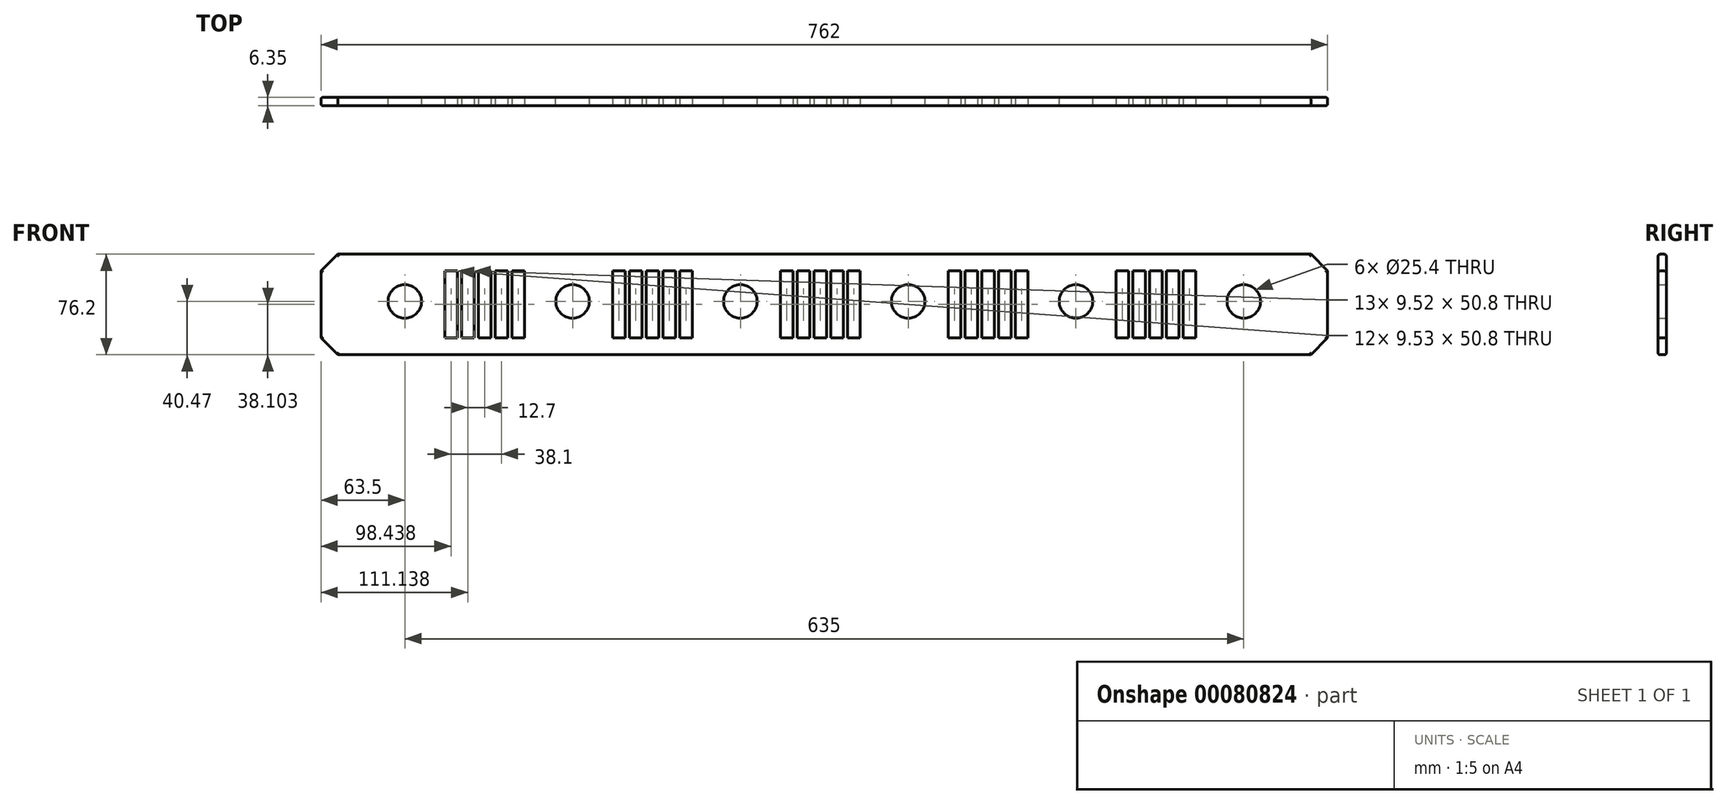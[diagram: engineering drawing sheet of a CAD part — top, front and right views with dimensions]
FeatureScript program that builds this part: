
annotation { "Feature Type Name" : "Feature", "Feature Type Description" : "" }
export const myFeature = defineFeature(function(context is Context, id is Id, definition is map)
    precondition{}
    {
        {
            var Q0;
            Q0=qCreatedBy(makeId("Front.planeOp"),FACE);
            var sketch = newSketch(context, id + "F0", { "sketchPlane" : qUnion([Q0])});
            skLineSegment(sketch, "E0.bottom", {"start": v(-63.5, 35.73) * mm, "end": v(698.5, 35.73) * mm});
            skLineSegment(sketch, "E0.top", {"start": v(-63.5, -40.47) * mm, "end": v(698.5, -40.47) * mm});
            skLineSegment(sketch, "E0.left", {"start": v(-63.5, 35.73) * mm, "end": v(-63.5, -40.47) * mm});
            skLineSegment(sketch, "E0.right", {"start": v(698.5, 35.73) * mm, "end": v(698.5, -40.47) * mm});
            skCircle(sketch, "E1", {"center": v(0, 0) * mm, "radius": 12.7 * mm});
            skCircle(sketch, "E2", {"center": v(127, 0) * mm, "radius": 12.7 * mm});
            skCircle(sketch, "E3", {"center": v(254, 0) * mm, "radius": 12.7 * mm});
            skCircle(sketch, "E4", {"center": v(381, 0) * mm, "radius": 12.7 * mm});
            skCircle(sketch, "E5", {"center": v(508, 0) * mm, "radius": 12.7 * mm});
            skCircle(sketch, "E6", {"center": v(635, 0) * mm, "radius": 12.7 * mm});
            skSolve(sketch);
        }
        {
            var Q0;
            Q0 = qSketchRegion(id + "F0", true);
            extrude(context, id + "F1", {"entities" : qUnion([Q0]), "depth" : 6.35 * mm});
        }
        {
            var Q0;
            Q0=makeQuery(id+"F1.opExtrude","CAP_FACE",FACE,{"disambiguationData":[OSD([sQuery(id+"F0.wireOp",EDGE,"E0.bottom"),sQuery(id+"F0.wireOp",EDGE,"E0.top"),sQuery(id+"F0.wireOp",EDGE,"E0.left"),sQuery(id+"F0.wireOp",EDGE,"E0.right"),sQuery(id+"F0.wireOp",EDGE,"E1"),sQuery(id+"F0.wireOp",EDGE,"E2"),sQuery(id+"F0.wireOp",EDGE,"E3"),sQuery(id+"F0.wireOp",EDGE,"E4"),sQuery(id+"F0.wireOp",EDGE,"E5"),sQuery(id+"F0.wireOp",EDGE,"E6")])],"isStart":false});
            var sketch = newSketch(context, id + "F2", { "sketchPlane" : qUnion([Q0])});
            skLineSegment(sketch, "E7.bottom", {"start": v(30.18, 23.03) * mm, "end": v(39.7, 23.03) * mm});
            skLineSegment(sketch, "E7.top", {"start": v(30.18, -27.77) * mm, "end": v(39.7, -27.77) * mm});
            skLineSegment(sketch, "E7.left", {"start": v(30.18, 23.03) * mm, "end": v(30.18, -27.77) * mm});
            skLineSegment(sketch, "E7.right", {"start": v(39.7, 23.03) * mm, "end": v(39.7, -27.77) * mm});
            skLineSegment(sketch, "E8.1.0.0", {"start": v(42.88, -27.77) * mm, "end": v(52.4, -27.77) * mm});
            skLineSegment(sketch, "E8.1.0.1", {"start": v(42.88, 23.03) * mm, "end": v(52.4, 23.03) * mm});
            skLineSegment(sketch, "E8.1.0.2", {"start": v(42.88, 23.03) * mm, "end": v(42.88, -27.77) * mm});
            skLineSegment(sketch, "E8.1.0.3", {"start": v(52.4, 23.03) * mm, "end": v(52.4, -27.77) * mm});
            skLineSegment(sketch, "E8.2.0.0", {"start": v(55.58, -27.77) * mm, "end": v(65.1, -27.77) * mm});
            skLineSegment(sketch, "E8.2.0.1", {"start": v(55.58, 23.03) * mm, "end": v(65.1, 23.03) * mm});
            skLineSegment(sketch, "E8.2.0.2", {"start": v(55.58, 23.03) * mm, "end": v(55.58, -27.77) * mm});
            skLineSegment(sketch, "E8.2.0.3", {"start": v(65.1, 23.03) * mm, "end": v(65.1, -27.77) * mm});
            skLineSegment(sketch, "E8.direction1", {"start": v(30.18, -27.77) * mm, "end": v(42.88, -27.77) * mm, "construction": true});
            skLineSegment(sketch, "E9.0.3.0", {"start": v(68.28, -27.77) * mm, "end": v(77.8, -27.77) * mm});
            skLineSegment(sketch, "E9.3.3.0", {"start": v(68.28, 23.03) * mm, "end": v(77.8, 23.03) * mm});
            skLineSegment(sketch, "E9.6.3.0", {"start": v(68.28, 23.03) * mm, "end": v(68.28, -27.77) * mm});
            skLineSegment(sketch, "E9.9.3.0", {"start": v(77.8, 23.03) * mm, "end": v(77.8, -27.77) * mm});
            skLineSegment(sketch, "E9.0.4.0", {"start": v(80.98, -27.77) * mm, "end": v(90.5, -27.77) * mm});
            skLineSegment(sketch, "E9.3.4.0", {"start": v(80.98, 23.03) * mm, "end": v(90.5, 23.03) * mm});
            skLineSegment(sketch, "E9.6.4.0", {"start": v(80.98, 23.03) * mm, "end": v(80.98, -27.77) * mm});
            skLineSegment(sketch, "E9.9.4.0", {"start": v(90.5, 23.03) * mm, "end": v(90.5, -27.77) * mm});
            skLineSegment(sketch, "E10.bottom", {"start": v(157.18, 23.03) * mm, "end": v(166.7, 23.03) * mm});
            skLineSegment(sketch, "E10.top", {"start": v(157.18, -27.77) * mm, "end": v(166.7, -27.77) * mm});
            skLineSegment(sketch, "E10.left", {"start": v(157.18, 23.03) * mm, "end": v(157.18, -27.77) * mm});
            skLineSegment(sketch, "E10.right", {"start": v(166.7, 23.03) * mm, "end": v(166.7, -27.77) * mm});
            skLineSegment(sketch, "E11.1.0.0", {"start": v(169.88, -27.77) * mm, "end": v(179.4, -27.77) * mm});
            skLineSegment(sketch, "E11.1.0.1", {"start": v(169.88, 23.03) * mm, "end": v(179.4, 23.03) * mm});
            skLineSegment(sketch, "E11.1.0.2", {"start": v(169.88, 23.03) * mm, "end": v(169.88, -27.77) * mm});
            skLineSegment(sketch, "E11.1.0.3", {"start": v(179.4, 23.03) * mm, "end": v(179.4, -27.77) * mm});
            skLineSegment(sketch, "E11.2.0.0", {"start": v(182.58, -27.77) * mm, "end": v(192.1, -27.77) * mm});
            skLineSegment(sketch, "E11.2.0.1", {"start": v(182.58, 23.03) * mm, "end": v(192.1, 23.03) * mm});
            skLineSegment(sketch, "E11.2.0.2", {"start": v(182.58, 23.03) * mm, "end": v(182.58, -27.77) * mm});
            skLineSegment(sketch, "E11.2.0.3", {"start": v(192.1, 23.03) * mm, "end": v(192.1, -27.77) * mm});
            skLineSegment(sketch, "E11.direction1", {"start": v(157.18, -27.77) * mm, "end": v(169.88, -27.77) * mm, "construction": true});
            skLineSegment(sketch, "E12.0.3.0", {"start": v(195.28, -27.77) * mm, "end": v(204.8, -27.77) * mm});
            skLineSegment(sketch, "E12.3.3.0", {"start": v(195.28, 23.03) * mm, "end": v(204.8, 23.03) * mm});
            skLineSegment(sketch, "E12.6.3.0", {"start": v(195.28, 23.03) * mm, "end": v(195.28, -27.77) * mm});
            skLineSegment(sketch, "E12.9.3.0", {"start": v(204.8, 23.03) * mm, "end": v(204.8, -27.77) * mm});
            skLineSegment(sketch, "E12.0.4.0", {"start": v(207.98, -27.77) * mm, "end": v(217.5, -27.77) * mm});
            skLineSegment(sketch, "E12.3.4.0", {"start": v(207.98, 23.03) * mm, "end": v(217.5, 23.03) * mm});
            skLineSegment(sketch, "E12.6.4.0", {"start": v(207.98, 23.03) * mm, "end": v(207.98, -27.77) * mm});
            skLineSegment(sketch, "E12.9.4.0", {"start": v(217.5, 23.03) * mm, "end": v(217.5, -27.77) * mm});
            skLineSegment(sketch, "E13.bottom", {"start": v(284.18, 23.03) * mm, "end": v(293.7, 23.03) * mm});
            skLineSegment(sketch, "E13.top", {"start": v(284.18, -27.77) * mm, "end": v(293.7, -27.77) * mm});
            skLineSegment(sketch, "E13.left", {"start": v(284.18, 23.03) * mm, "end": v(284.18, -27.77) * mm});
            skLineSegment(sketch, "E13.right", {"start": v(293.7, 23.03) * mm, "end": v(293.7, -27.77) * mm});
            skLineSegment(sketch, "E14.1.0.0", {"start": v(296.88, -27.77) * mm, "end": v(306.4, -27.77) * mm});
            skLineSegment(sketch, "E14.1.0.1", {"start": v(296.88, 23.03) * mm, "end": v(306.4, 23.03) * mm});
            skLineSegment(sketch, "E14.1.0.2", {"start": v(296.88, 23.03) * mm, "end": v(296.88, -27.77) * mm});
            skLineSegment(sketch, "E14.1.0.3", {"start": v(306.4, 23.03) * mm, "end": v(306.4, -27.77) * mm});
            skLineSegment(sketch, "E14.2.0.0", {"start": v(309.58, -27.77) * mm, "end": v(319.1, -27.77) * mm});
            skLineSegment(sketch, "E14.2.0.1", {"start": v(309.58, 23.03) * mm, "end": v(319.1, 23.03) * mm});
            skLineSegment(sketch, "E14.2.0.2", {"start": v(309.58, 23.03) * mm, "end": v(309.58, -27.77) * mm});
            skLineSegment(sketch, "E14.2.0.3", {"start": v(319.1, 23.03) * mm, "end": v(319.1, -27.77) * mm});
            skLineSegment(sketch, "E14.direction1", {"start": v(284.18, -27.77) * mm, "end": v(296.88, -27.77) * mm, "construction": true});
            skLineSegment(sketch, "E15.0.3.0", {"start": v(322.28, -27.77) * mm, "end": v(331.8, -27.77) * mm});
            skLineSegment(sketch, "E15.3.3.0", {"start": v(322.28, 23.03) * mm, "end": v(331.8, 23.03) * mm});
            skLineSegment(sketch, "E15.6.3.0", {"start": v(322.28, 23.03) * mm, "end": v(322.28, -27.77) * mm});
            skLineSegment(sketch, "E15.9.3.0", {"start": v(331.8, 23.03) * mm, "end": v(331.8, -27.77) * mm});
            skLineSegment(sketch, "E15.0.4.0", {"start": v(334.98, -27.77) * mm, "end": v(344.5, -27.77) * mm});
            skLineSegment(sketch, "E15.3.4.0", {"start": v(334.98, 23.03) * mm, "end": v(344.5, 23.03) * mm});
            skLineSegment(sketch, "E15.6.4.0", {"start": v(334.98, 23.03) * mm, "end": v(334.98, -27.77) * mm});
            skLineSegment(sketch, "E15.9.4.0", {"start": v(344.5, 23.03) * mm, "end": v(344.5, -27.77) * mm});
            skLineSegment(sketch, "E16.bottom", {"start": v(411.18, 23.03) * mm, "end": v(420.7, 23.03) * mm});
            skLineSegment(sketch, "E16.top", {"start": v(411.18, -27.77) * mm, "end": v(420.7, -27.77) * mm});
            skLineSegment(sketch, "E16.left", {"start": v(411.18, 23.03) * mm, "end": v(411.18, -27.77) * mm});
            skLineSegment(sketch, "E16.right", {"start": v(420.7, 23.03) * mm, "end": v(420.7, -27.77) * mm});
            skLineSegment(sketch, "E17.1.0.0", {"start": v(423.88, -27.77) * mm, "end": v(433.4, -27.77) * mm});
            skLineSegment(sketch, "E17.1.0.1", {"start": v(423.88, 23.03) * mm, "end": v(433.4, 23.03) * mm});
            skLineSegment(sketch, "E17.1.0.2", {"start": v(423.88, 23.03) * mm, "end": v(423.88, -27.77) * mm});
            skLineSegment(sketch, "E17.1.0.3", {"start": v(433.4, 23.03) * mm, "end": v(433.4, -27.77) * mm});
            skLineSegment(sketch, "E17.2.0.0", {"start": v(436.58, -27.77) * mm, "end": v(446.1, -27.77) * mm});
            skLineSegment(sketch, "E17.2.0.1", {"start": v(436.58, 23.03) * mm, "end": v(446.1, 23.03) * mm});
            skLineSegment(sketch, "E17.2.0.2", {"start": v(436.58, 23.03) * mm, "end": v(436.58, -27.77) * mm});
            skLineSegment(sketch, "E17.2.0.3", {"start": v(446.1, 23.03) * mm, "end": v(446.1, -27.77) * mm});
            skLineSegment(sketch, "E17.direction1", {"start": v(411.18, -27.77) * mm, "end": v(423.88, -27.77) * mm, "construction": true});
            skLineSegment(sketch, "E18.0.3.0", {"start": v(449.28, -27.77) * mm, "end": v(458.8, -27.77) * mm});
            skLineSegment(sketch, "E18.3.3.0", {"start": v(449.28, 23.03) * mm, "end": v(458.8, 23.03) * mm});
            skLineSegment(sketch, "E18.6.3.0", {"start": v(449.28, 23.03) * mm, "end": v(449.28, -27.77) * mm});
            skLineSegment(sketch, "E18.9.3.0", {"start": v(458.8, 23.03) * mm, "end": v(458.8, -27.77) * mm});
            skLineSegment(sketch, "E18.0.4.0", {"start": v(461.98, -27.77) * mm, "end": v(471.5, -27.77) * mm});
            skLineSegment(sketch, "E18.3.4.0", {"start": v(461.98, 23.03) * mm, "end": v(471.5, 23.03) * mm});
            skLineSegment(sketch, "E18.6.4.0", {"start": v(461.98, 23.03) * mm, "end": v(461.98, -27.77) * mm});
            skLineSegment(sketch, "E18.9.4.0", {"start": v(471.5, 23.03) * mm, "end": v(471.5, -27.77) * mm});
            skLineSegment(sketch, "E19.bottom", {"start": v(538.18, 23.03) * mm, "end": v(547.7, 23.03) * mm});
            skLineSegment(sketch, "E19.top", {"start": v(538.18, -27.77) * mm, "end": v(547.7, -27.77) * mm});
            skLineSegment(sketch, "E19.left", {"start": v(538.18, 23.03) * mm, "end": v(538.18, -27.77) * mm});
            skLineSegment(sketch, "E19.right", {"start": v(547.7, 23.03) * mm, "end": v(547.7, -27.77) * mm});
            skLineSegment(sketch, "E20.1.0.0", {"start": v(550.88, -27.77) * mm, "end": v(560.4, -27.77) * mm});
            skLineSegment(sketch, "E20.1.0.1", {"start": v(550.88, 23.03) * mm, "end": v(560.4, 23.03) * mm});
            skLineSegment(sketch, "E20.1.0.2", {"start": v(550.88, 23.03) * mm, "end": v(550.88, -27.77) * mm});
            skLineSegment(sketch, "E20.1.0.3", {"start": v(560.4, 23.03) * mm, "end": v(560.4, -27.77) * mm});
            skLineSegment(sketch, "E20.2.0.0", {"start": v(563.58, -27.77) * mm, "end": v(573.1, -27.77) * mm});
            skLineSegment(sketch, "E20.2.0.1", {"start": v(563.58, 23.03) * mm, "end": v(573.1, 23.03) * mm});
            skLineSegment(sketch, "E20.2.0.2", {"start": v(563.58, 23.03) * mm, "end": v(563.58, -27.77) * mm});
            skLineSegment(sketch, "E20.2.0.3", {"start": v(573.1, 23.03) * mm, "end": v(573.1, -27.77) * mm});
            skLineSegment(sketch, "E20.direction1", {"start": v(538.18, -27.77) * mm, "end": v(550.88, -27.77) * mm, "construction": true});
            skLineSegment(sketch, "E21.0.3.0", {"start": v(576.28, -27.77) * mm, "end": v(585.8, -27.77) * mm});
            skLineSegment(sketch, "E21.3.3.0", {"start": v(576.28, 23.03) * mm, "end": v(585.8, 23.03) * mm});
            skLineSegment(sketch, "E21.6.3.0", {"start": v(576.28, 23.03) * mm, "end": v(576.28, -27.77) * mm});
            skLineSegment(sketch, "E21.9.3.0", {"start": v(585.8, 23.03) * mm, "end": v(585.8, -27.77) * mm});
            skLineSegment(sketch, "E21.0.4.0", {"start": v(588.98, -27.77) * mm, "end": v(598.5, -27.77) * mm});
            skLineSegment(sketch, "E21.3.4.0", {"start": v(588.98, 23.03) * mm, "end": v(598.5, 23.03) * mm});
            skLineSegment(sketch, "E21.6.4.0", {"start": v(588.98, 23.03) * mm, "end": v(588.98, -27.77) * mm});
            skLineSegment(sketch, "E21.9.4.0", {"start": v(598.5, 23.03) * mm, "end": v(598.5, -27.77) * mm});
            skSolve(sketch);
        }
        {
            var Q0;
            Q0 = qSketchRegion(id + "F2", true);
            extrude(context, id + "F3", {"entities" : qUnion([Q0]), "operationType" : NewBodyOperationType.REMOVE, "endBound" : BoundingType.THROUGH_ALL, "oppositeDirection" : true, "depth" : 25.4 * mm});
        }
        {
            var Q0;
            Q0=makeQuery(id+"F1.opExtrude","SWEPT_EDGE",EDGE,{"disambiguationData":[OSD([sQuery(id+"F0.wireOp",EDGE,"E0.bottom"),sQuery(id+"F0.wireOp",EDGE,"E0.left")])]});
            var Q1;
            Q1=makeQuery(id+"F1.opExtrude","SWEPT_EDGE",EDGE,{"disambiguationData":[OSD([sQuery(id+"F0.wireOp",EDGE,"E0.top"),sQuery(id+"F0.wireOp",EDGE,"E0.left")])]});
            var Q2;
            Q2=makeQuery(id+"F1.opExtrude","SWEPT_EDGE",EDGE,{"disambiguationData":[OSD([sQuery(id+"F0.wireOp",EDGE,"E0.bottom"),sQuery(id+"F0.wireOp",EDGE,"E0.right")])]});
            var Q3;
            Q3=makeQuery(id+"F1.opExtrude","SWEPT_EDGE",EDGE,{"disambiguationData":[OSD([sQuery(id+"F0.wireOp",EDGE,"E0.top"),sQuery(id+"F0.wireOp",EDGE,"E0.right")])]});
            chamfer(context, id + "F4", {"entities" : qUnion([Q0, Q1, Q2, Q3]), "width" : 12.7 * mm, "tangentPropagation" : true});
        }
        {
            var Q0;
            Q0=makeQuery(id+"F1.opExtrude","CAP_EDGE",EDGE,{"disambiguationData":[OSD([sQuery(id+"F0.wireOp",EDGE,"E0.bottom")])],"isStart":false});
            var Q1;
            Q1=makeQuery(id+"F1.opExtrude","CAP_EDGE",EDGE,{"disambiguationData":[OSD([sQuery(id+"F0.wireOp",EDGE,"E0.bottom")])],"isStart":true});
            var Q2;
            Q2=makeQuery(id+"F1.opExtrude","CAP_EDGE",EDGE,{"disambiguationData":[OSD([sQuery(id+"F0.wireOp",EDGE,"E0.top")])],"isStart":false});
            var Q3;
            Q3=makeQuery(id+"F1.opExtrude","CAP_EDGE",EDGE,{"disambiguationData":[OSD([sQuery(id+"F0.wireOp",EDGE,"E0.top")])],"isStart":true});
            var Q4;
            Q4=makeQuery(id+"F1.opExtrude","CAP_EDGE",EDGE,{"disambiguationData":[OSD([sQuery(id+"F0.wireOp",EDGE,"E0.left")])],"isStart":false});
            var Q5;
            Q5=makeQuery(id+"F1.opExtrude","CAP_EDGE",EDGE,{"disambiguationData":[OSD([sQuery(id+"F0.wireOp",EDGE,"E0.left")])],"isStart":true});
            var Q6;
            Q6=makeQuery(id+"F1.opExtrude","CAP_EDGE",EDGE,{"disambiguationData":[OSD([sQuery(id+"F0.wireOp",EDGE,"E0.right")])],"isStart":false});
            var Q7;
            Q7=makeQuery(id+"F1.opExtrude","CAP_EDGE",EDGE,{"disambiguationData":[OSD([sQuery(id+"F0.wireOp",EDGE,"E0.right")])],"isStart":true});
            var Q8;
            {var subQ0=sQuery(id+"F0.wireOp",EDGE,"E0.left");var subQ1=sQuery(id+"F0.wireOp",EDGE,"E0.top");Q8=makeQuery(id+"F4.opChamfer","BLEND_EDGE",EDGE,{"blendedFrom":[makeQuery(id+"F1.opExtrude","SWEPT_EDGE",EDGE,{"disambiguationData":[OSD([subQ1,subQ0])]}),makeQuery(id+"F1.opExtrude","CAP_FACE",FACE,{"disambiguationData":[OSD([sQuery(id+"F0.wireOp",EDGE,"E0.bottom"),subQ1,subQ0,sQuery(id+"F0.wireOp",EDGE,"E0.right"),sQuery(id+"F0.wireOp",EDGE,"E1"),sQuery(id+"F0.wireOp",EDGE,"E2"),sQuery(id+"F0.wireOp",EDGE,"E3"),sQuery(id+"F0.wireOp",EDGE,"E4"),sQuery(id+"F0.wireOp",EDGE,"E5"),sQuery(id+"F0.wireOp",EDGE,"E6")])],"isStart":false})],"blendedInto":[makeQuery(id+"F1.opExtrude","CAP_FACE",FACE,{"disambiguationData":[OSD([sQuery(id+"F0.wireOp",EDGE,"E0.bottom"),subQ1,subQ0,sQuery(id+"F0.wireOp",EDGE,"E0.right"),sQuery(id+"F0.wireOp",EDGE,"E1"),sQuery(id+"F0.wireOp",EDGE,"E2"),sQuery(id+"F0.wireOp",EDGE,"E3"),sQuery(id+"F0.wireOp",EDGE,"E4"),sQuery(id+"F0.wireOp",EDGE,"E5"),sQuery(id+"F0.wireOp",EDGE,"E6")])],"isStart":false})]});}
            var Q9;
            {var subQ0=sQuery(id+"F0.wireOp",EDGE,"E0.left");var subQ1=sQuery(id+"F0.wireOp",EDGE,"E0.top");Q9=makeQuery(id+"F4.opChamfer","BLEND_EDGE",EDGE,{"blendedFrom":[makeQuery(id+"F1.opExtrude","SWEPT_EDGE",EDGE,{"disambiguationData":[OSD([subQ1,subQ0])]}),makeQuery(id+"F1.opExtrude","CAP_FACE",FACE,{"disambiguationData":[OSD([sQuery(id+"F0.wireOp",EDGE,"E0.bottom"),subQ1,subQ0,sQuery(id+"F0.wireOp",EDGE,"E0.right"),sQuery(id+"F0.wireOp",EDGE,"E1"),sQuery(id+"F0.wireOp",EDGE,"E2"),sQuery(id+"F0.wireOp",EDGE,"E3"),sQuery(id+"F0.wireOp",EDGE,"E4"),sQuery(id+"F0.wireOp",EDGE,"E5"),sQuery(id+"F0.wireOp",EDGE,"E6")])],"isStart":true})],"blendedInto":[makeQuery(id+"F1.opExtrude","CAP_FACE",FACE,{"disambiguationData":[OSD([sQuery(id+"F0.wireOp",EDGE,"E0.bottom"),subQ1,subQ0,sQuery(id+"F0.wireOp",EDGE,"E0.right"),sQuery(id+"F0.wireOp",EDGE,"E1"),sQuery(id+"F0.wireOp",EDGE,"E2"),sQuery(id+"F0.wireOp",EDGE,"E3"),sQuery(id+"F0.wireOp",EDGE,"E4"),sQuery(id+"F0.wireOp",EDGE,"E5"),sQuery(id+"F0.wireOp",EDGE,"E6")])],"isStart":true})]});}
            var Q10;
            {var subQ0=sQuery(id+"F0.wireOp",EDGE,"E0.right");var subQ1=sQuery(id+"F0.wireOp",EDGE,"E0.bottom");Q10=makeQuery(id+"F4.opChamfer","BLEND_EDGE",EDGE,{"blendedFrom":[makeQuery(id+"F1.opExtrude","SWEPT_EDGE",EDGE,{"disambiguationData":[OSD([subQ1,subQ0])]}),makeQuery(id+"F1.opExtrude","CAP_FACE",FACE,{"disambiguationData":[OSD([subQ1,sQuery(id+"F0.wireOp",EDGE,"E0.top"),sQuery(id+"F0.wireOp",EDGE,"E0.left"),subQ0,sQuery(id+"F0.wireOp",EDGE,"E1"),sQuery(id+"F0.wireOp",EDGE,"E2"),sQuery(id+"F0.wireOp",EDGE,"E3"),sQuery(id+"F0.wireOp",EDGE,"E4"),sQuery(id+"F0.wireOp",EDGE,"E5"),sQuery(id+"F0.wireOp",EDGE,"E6")])],"isStart":false})],"blendedInto":[makeQuery(id+"F1.opExtrude","CAP_FACE",FACE,{"disambiguationData":[OSD([subQ1,sQuery(id+"F0.wireOp",EDGE,"E0.top"),sQuery(id+"F0.wireOp",EDGE,"E0.left"),subQ0,sQuery(id+"F0.wireOp",EDGE,"E1"),sQuery(id+"F0.wireOp",EDGE,"E2"),sQuery(id+"F0.wireOp",EDGE,"E3"),sQuery(id+"F0.wireOp",EDGE,"E4"),sQuery(id+"F0.wireOp",EDGE,"E5"),sQuery(id+"F0.wireOp",EDGE,"E6")])],"isStart":false})]});}
            var Q11;
            {var subQ0=sQuery(id+"F0.wireOp",EDGE,"E0.right");var subQ1=sQuery(id+"F0.wireOp",EDGE,"E0.bottom");Q11=makeQuery(id+"F4.opChamfer","BLEND_EDGE",EDGE,{"blendedFrom":[makeQuery(id+"F1.opExtrude","SWEPT_EDGE",EDGE,{"disambiguationData":[OSD([subQ1,subQ0])]}),makeQuery(id+"F1.opExtrude","CAP_FACE",FACE,{"disambiguationData":[OSD([subQ1,sQuery(id+"F0.wireOp",EDGE,"E0.top"),sQuery(id+"F0.wireOp",EDGE,"E0.left"),subQ0,sQuery(id+"F0.wireOp",EDGE,"E1"),sQuery(id+"F0.wireOp",EDGE,"E2"),sQuery(id+"F0.wireOp",EDGE,"E3"),sQuery(id+"F0.wireOp",EDGE,"E4"),sQuery(id+"F0.wireOp",EDGE,"E5"),sQuery(id+"F0.wireOp",EDGE,"E6")])],"isStart":true})],"blendedInto":[makeQuery(id+"F1.opExtrude","CAP_FACE",FACE,{"disambiguationData":[OSD([subQ1,sQuery(id+"F0.wireOp",EDGE,"E0.top"),sQuery(id+"F0.wireOp",EDGE,"E0.left"),subQ0,sQuery(id+"F0.wireOp",EDGE,"E1"),sQuery(id+"F0.wireOp",EDGE,"E2"),sQuery(id+"F0.wireOp",EDGE,"E3"),sQuery(id+"F0.wireOp",EDGE,"E4"),sQuery(id+"F0.wireOp",EDGE,"E5"),sQuery(id+"F0.wireOp",EDGE,"E6")])],"isStart":true})]});}
            var Q12;
            {var subQ0=sQuery(id+"F0.wireOp",EDGE,"E0.right");var subQ1=sQuery(id+"F0.wireOp",EDGE,"E0.top");Q12=makeQuery(id+"F4.opChamfer","BLEND_EDGE",EDGE,{"blendedFrom":[makeQuery(id+"F1.opExtrude","SWEPT_EDGE",EDGE,{"disambiguationData":[OSD([subQ1,subQ0])]}),makeQuery(id+"F1.opExtrude","CAP_FACE",FACE,{"disambiguationData":[OSD([sQuery(id+"F0.wireOp",EDGE,"E0.bottom"),subQ1,sQuery(id+"F0.wireOp",EDGE,"E0.left"),subQ0,sQuery(id+"F0.wireOp",EDGE,"E1"),sQuery(id+"F0.wireOp",EDGE,"E2"),sQuery(id+"F0.wireOp",EDGE,"E3"),sQuery(id+"F0.wireOp",EDGE,"E4"),sQuery(id+"F0.wireOp",EDGE,"E5"),sQuery(id+"F0.wireOp",EDGE,"E6")])],"isStart":false})],"blendedInto":[makeQuery(id+"F1.opExtrude","CAP_FACE",FACE,{"disambiguationData":[OSD([sQuery(id+"F0.wireOp",EDGE,"E0.bottom"),subQ1,sQuery(id+"F0.wireOp",EDGE,"E0.left"),subQ0,sQuery(id+"F0.wireOp",EDGE,"E1"),sQuery(id+"F0.wireOp",EDGE,"E2"),sQuery(id+"F0.wireOp",EDGE,"E3"),sQuery(id+"F0.wireOp",EDGE,"E4"),sQuery(id+"F0.wireOp",EDGE,"E5"),sQuery(id+"F0.wireOp",EDGE,"E6")])],"isStart":false})]});}
            var Q13;
            {var subQ0=sQuery(id+"F0.wireOp",EDGE,"E0.right");var subQ1=sQuery(id+"F0.wireOp",EDGE,"E0.top");Q13=makeQuery(id+"F4.opChamfer","BLEND_EDGE",EDGE,{"blendedFrom":[makeQuery(id+"F1.opExtrude","SWEPT_EDGE",EDGE,{"disambiguationData":[OSD([subQ1,subQ0])]}),makeQuery(id+"F1.opExtrude","CAP_FACE",FACE,{"disambiguationData":[OSD([sQuery(id+"F0.wireOp",EDGE,"E0.bottom"),subQ1,sQuery(id+"F0.wireOp",EDGE,"E0.left"),subQ0,sQuery(id+"F0.wireOp",EDGE,"E1"),sQuery(id+"F0.wireOp",EDGE,"E2"),sQuery(id+"F0.wireOp",EDGE,"E3"),sQuery(id+"F0.wireOp",EDGE,"E4"),sQuery(id+"F0.wireOp",EDGE,"E5"),sQuery(id+"F0.wireOp",EDGE,"E6")])],"isStart":true})],"blendedInto":[makeQuery(id+"F1.opExtrude","CAP_FACE",FACE,{"disambiguationData":[OSD([sQuery(id+"F0.wireOp",EDGE,"E0.bottom"),subQ1,sQuery(id+"F0.wireOp",EDGE,"E0.left"),subQ0,sQuery(id+"F0.wireOp",EDGE,"E1"),sQuery(id+"F0.wireOp",EDGE,"E2"),sQuery(id+"F0.wireOp",EDGE,"E3"),sQuery(id+"F0.wireOp",EDGE,"E4"),sQuery(id+"F0.wireOp",EDGE,"E5"),sQuery(id+"F0.wireOp",EDGE,"E6")])],"isStart":true})]});}
            var Q14;
            {var subQ0=sQuery(id+"F0.wireOp",EDGE,"E0.left");var subQ1=sQuery(id+"F0.wireOp",EDGE,"E0.bottom");Q14=makeQuery(id+"F4.opChamfer","BLEND_EDGE",EDGE,{"blendedFrom":[makeQuery(id+"F1.opExtrude","SWEPT_EDGE",EDGE,{"disambiguationData":[OSD([subQ1,subQ0])]}),makeQuery(id+"F1.opExtrude","CAP_FACE",FACE,{"disambiguationData":[OSD([subQ1,sQuery(id+"F0.wireOp",EDGE,"E0.top"),subQ0,sQuery(id+"F0.wireOp",EDGE,"E0.right"),sQuery(id+"F0.wireOp",EDGE,"E1"),sQuery(id+"F0.wireOp",EDGE,"E2"),sQuery(id+"F0.wireOp",EDGE,"E3"),sQuery(id+"F0.wireOp",EDGE,"E4"),sQuery(id+"F0.wireOp",EDGE,"E5"),sQuery(id+"F0.wireOp",EDGE,"E6")])],"isStart":false})],"blendedInto":[makeQuery(id+"F1.opExtrude","CAP_FACE",FACE,{"disambiguationData":[OSD([subQ1,sQuery(id+"F0.wireOp",EDGE,"E0.top"),subQ0,sQuery(id+"F0.wireOp",EDGE,"E0.right"),sQuery(id+"F0.wireOp",EDGE,"E1"),sQuery(id+"F0.wireOp",EDGE,"E2"),sQuery(id+"F0.wireOp",EDGE,"E3"),sQuery(id+"F0.wireOp",EDGE,"E4"),sQuery(id+"F0.wireOp",EDGE,"E5"),sQuery(id+"F0.wireOp",EDGE,"E6")])],"isStart":false})]});}
            var Q15;
            {var subQ0=sQuery(id+"F0.wireOp",EDGE,"E0.left");var subQ1=sQuery(id+"F0.wireOp",EDGE,"E0.bottom");Q15=makeQuery(id+"F4.opChamfer","BLEND_EDGE",EDGE,{"blendedFrom":[makeQuery(id+"F1.opExtrude","SWEPT_EDGE",EDGE,{"disambiguationData":[OSD([subQ1,subQ0])]}),makeQuery(id+"F1.opExtrude","CAP_FACE",FACE,{"disambiguationData":[OSD([subQ1,sQuery(id+"F0.wireOp",EDGE,"E0.top"),subQ0,sQuery(id+"F0.wireOp",EDGE,"E0.right"),sQuery(id+"F0.wireOp",EDGE,"E1"),sQuery(id+"F0.wireOp",EDGE,"E2"),sQuery(id+"F0.wireOp",EDGE,"E3"),sQuery(id+"F0.wireOp",EDGE,"E4"),sQuery(id+"F0.wireOp",EDGE,"E5"),sQuery(id+"F0.wireOp",EDGE,"E6")])],"isStart":true})],"blendedInto":[makeQuery(id+"F1.opExtrude","CAP_FACE",FACE,{"disambiguationData":[OSD([subQ1,sQuery(id+"F0.wireOp",EDGE,"E0.top"),subQ0,sQuery(id+"F0.wireOp",EDGE,"E0.right"),sQuery(id+"F0.wireOp",EDGE,"E1"),sQuery(id+"F0.wireOp",EDGE,"E2"),sQuery(id+"F0.wireOp",EDGE,"E3"),sQuery(id+"F0.wireOp",EDGE,"E4"),sQuery(id+"F0.wireOp",EDGE,"E5"),sQuery(id+"F0.wireOp",EDGE,"E6")])],"isStart":true})]});}
            fillet(context, id + "F5", {"entities" : qUnion([Q0, Q1, Q2, Q3, Q4, Q5, Q6, Q7, Q8, Q9, Q10, Q11, Q12, Q13, Q14, Q15]), "radius" : 1.6 * mm, "tangentPropagation" : true, "allowEdgeOverflow" : false});
        }
    });
